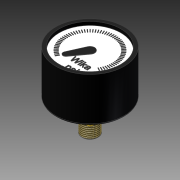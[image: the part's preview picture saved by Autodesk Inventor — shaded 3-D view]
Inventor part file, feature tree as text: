
AUTODESK INVENTOR PART (.ipt)
format: ipt  version: 2014 SP1 (Build 180222100, 222)  size: 651,776 bytes
history: native  units: mm (DEFAULTED — no unit token found)
features: extrude x6, sketch x6, thread x1, chamfer x1, fillet x1
ambient origin geometry x8: Origin, YZ Plane, XZ Plane, XY Plane, X Axis, Y Axis, Z Axis, Center Point
bodies: Solid1 (feature_tree)
feature tree (15):
  extrude  "Extrusion13"  Depth=26.0mm TaperAngle=0.0deg
  extrude  "Extrusion15"  Depth=14.0mm
  extrude  "Extrusion16"  Depth=10.0mm TaperAngle=0.0deg
  thread  "Thread3"  [1 undecoded]
  extrude  "Extrusion18"  Depth=10.0mm
  extrude  "Extrusion19"  Depth=0.5mm TaperAngle=45.0deg
  sketch  "Sketch19"  dims[d67=2.0mm d68=0.0mm d69=0.5mm d70=2.0mm d71=45.0deg]
  chamfer  "Chamfer1"  Distance=10.0mm
  fillet  "Fillet5"  Radius=3.0mm
  extrude  "Extrusion20"  Depth=0.2mm
  sketch  "Sketch13"  dims[d46=40.0mm d47=26.0mm d48=0.0mm]
  sketch  "Sketch15"  dims[d52=14.0mm d53=14.0mm]
  sketch  "Sketch16"  dims[d54=8.0mm d55=0.0mm d56=10.0mm d57=0.0mm d58=9.525mm]
  sketch  "Sketch18"  dims[d59=10.0mm d60=0.0mm d66=2.0mm]
  sketch  "Sketch20"  dims[d72=1.0mm d73=10.0mm d74=0.0mm d75=3.0mm d76=30.0mm d77=120.0deg d78=0.25mm d79=2.0mm d80=600.0mm d82=270.0deg d87=2.683433mm d88=0.2mm d89=0.0mm d91=9.0mm]
note: 1 required parameter value undecoded (feature->parameter linkage not recoverable at this tier; creation-order binding heuristic only, values carry confidence <= 0.55)
